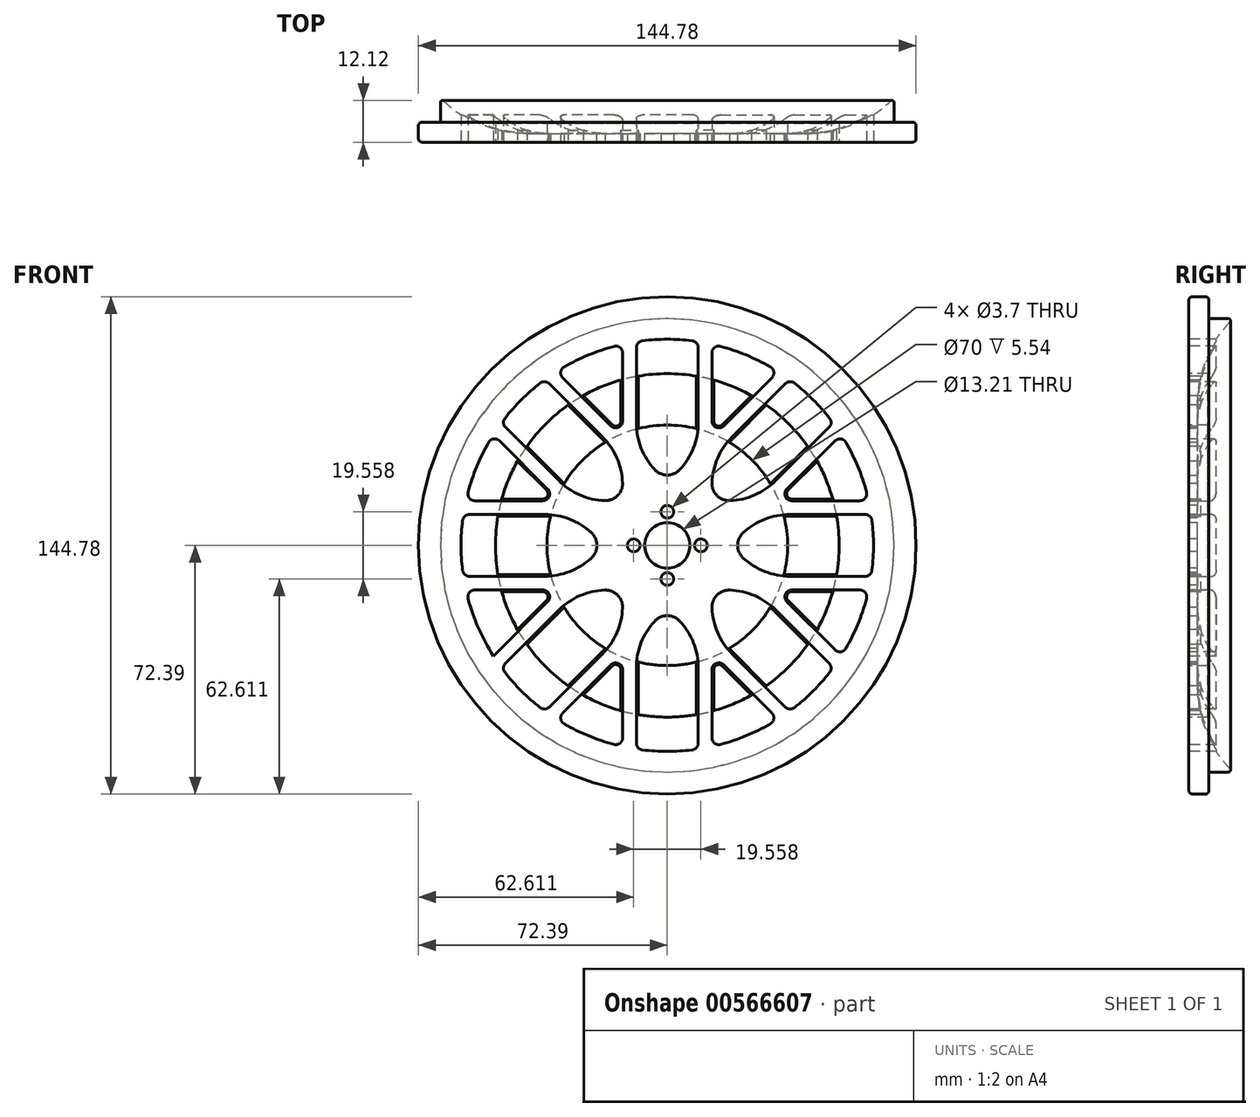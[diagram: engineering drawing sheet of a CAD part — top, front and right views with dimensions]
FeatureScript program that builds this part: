
annotation { "Feature Type Name" : "Feature", "Feature Type Description" : "" }
export const myFeature = defineFeature(function(context is Context, id is Id, definition is map)
    precondition{}
    {
        {
            var Q0;
            Q0=qCreatedBy(makeId("Right.planeOp"),FACE);
            var sketch = newSketch(context, id + "F0", { "sketchPlane" : qUnion([Q0])});
            skLineSegment(sketch, "E0", {"start": v(0, 6.6) * mm, "end": v(2.54, 6.6) * mm});
            skLineSegment(sketch, "E1", {"start": v(2.54, 6.6) * mm, "end": v(2.54, 42) * mm});
            skLineSegment(sketch, "E2", {"start": v(0, 6.6) * mm, "end": v(0, 66) * mm});
            skLineSegment(sketch, "E3", {"start": v(0, 66) * mm, "end": v(13, 66) * mm});
            skArc(sketch, "E4", {"start": v(2.54, 42) * mm, "mid": v(5.27, 55.1) * mm, "end": v(13, 66) * mm});
            skLineSegment(sketch, "E5", {"start": v(0, 0) * mm, "end": v(13, 0) * mm, "construction": true});
            skSolve(sketch);
        }
        {
            var Q0;
            Q0=makeQuery(id+"F0.imprint","IMPRINT",FACE,{"disambiguationData":[TD([[makeQuery(id+"F0.imprint","IMPRINT",EDGE,{"derivedFrom":sQuery(id+"F0.wireOp",EDGE,"E0")}),1.0]])]});
            var Q1;
            Q1=sQuery(id+"F0.wireOp",EDGE,"E5");
            revolve(context, id + "F1", {"entities" : qUnion([Q0]), "axis" : qUnion([Q1]), "revolveType" : RevolveType.FULL});
        }
        {
            var Q0;
            Q0=qCreatedBy(makeId("Front.planeOp"),FACE);
            var sketch = newSketch(context, id + "F2", { "sketchPlane" : qUnion([Q0])});
            skCircle(sketch, "E6", {"center": v(0, 0) * mm, "radius": 9.78 * mm, "construction": true});
            skPoint(sketch, "E7", {"position": v(0, 9.78) * mm});
            skPoint(sketch, "E8", {"position": v(0, -9.78) * mm});
            skPoint(sketch, "E9", {"position": v(9.78, 0) * mm});
            skPoint(sketch, "E10", {"position": v(-9.78, 0) * mm});
            skSolve(sketch);
        }
        {
            var Q0;
            Q0=sQuery(id+"F2.wireOp",VERTEX,"E7");
            var Q1;
            Q1=sQuery(id+"F2.wireOp",VERTEX,"E9");
            var Q2;
            Q2=sQuery(id+"F2.wireOp",VERTEX,"E8");
            var Q3;
            Q3=sQuery(id+"F2.wireOp",VERTEX,"E10");
            var Q4;
            Q4=makeQuery(id+"F1.opRevolve","SWEPT_BODY",BODY,{"disambiguationData":[OSD([sQuery(id+"F0.wireOp",EDGE,"E0"),sQuery(id+"F0.wireOp",EDGE,"E1"),sQuery(id+"F0.wireOp",EDGE,"E2"),sQuery(id+"F0.wireOp",EDGE,"E3"),sQuery(id+"F0.wireOp",EDGE,"E4")])]});
            hole(context, id + "F3", {"style" : HoleStyle.SIMPLE, "holeDiameter" : 3.7 * mm, "endStyle" : HoleEndStyle.THROUGH, "locations" : qUnion([Q0, Q1, Q2, Q3]), "scope" : qUnion([Q4])});
        }
        {
            var Q0;
            Q0=makeQuery(id+"F1.opRevolve","SWEPT_FACE",FACE,{"disambiguationData":[OSD([sQuery(id+"F0.wireOp",EDGE,"E2")])]});
            var sketch = newSketch(context, id + "F4", { "sketchPlane" : qUnion([Q0])});
            skArc(sketch, "E11", {"start": v(-35.58, 48.31) * mm, "mid": v(-42.43, 42.43) * mm, "end": v(-48.31, 35.58) * mm});
            skLineSegment(sketch, "E12", {"start": v(-58.57, 13) * mm, "end": v(-31.38, 13) * mm});
            skLineSegment(sketch, "E13", {"start": v(-58.57, -13) * mm, "end": v(-31.38, -13) * mm});
            skLineSegment(sketch, "E14", {"start": v(-13, 58.57) * mm, "end": v(-13, 31.38) * mm});
            skLineSegment(sketch, "E15", {"start": v(13, -58.57) * mm, "end": v(13, -31.38) * mm});
            skLineSegment(sketch, "E16", {"start": v(-50.61, 32.23) * mm, "end": v(-31.38, 13) * mm});
            skLineSegment(sketch, "E17", {"start": v(-32.23, 50.61) * mm, "end": v(-13, 31.38) * mm});
            skLineSegment(sketch, "E18", {"start": v(-50.61, -32.23) * mm, "end": v(-31.38, -13) * mm});
            skLineSegment(sketch, "E19", {"start": v(-32.23, -50.61) * mm, "end": v(-13, -31.38) * mm});
            skLineSegment(sketch, "E20.trimOffspring", {"start": v(0, 18.38) * mm, "end": v(9, 27.38) * mm});
            skLineSegment(sketch, "E21.trimOffspring", {"start": v(13, 13) * mm, "end": v(25.73, 13) * mm});
            skLineSegment(sketch, "E22.trimOffspring", {"start": v(18.38, 0) * mm, "end": v(27.38, -9) * mm});
            skLineSegment(sketch, "E23.trimOffspring", {"start": v(13, 13) * mm, "end": v(13, 25.73) * mm});
            skLineSegment(sketch, "E24.trimOffspring", {"start": v(18.38, 0) * mm, "end": v(27.38, 9) * mm});
            skLineSegment(sketch, "E25.trimOffspring", {"start": v(13, -13) * mm, "end": v(25.73, -13) * mm});
            skLineSegment(sketch, "E26.trimOffspring", {"start": v(0, -18.38) * mm, "end": v(9, -27.38) * mm});
            skLineSegment(sketch, "E27.trimOffspring", {"start": v(-13, -13) * mm, "end": v(-13, -25.73) * mm});
            skLineSegment(sketch, "E28.0", {"start": v(-35.58, 48.31) * mm, "end": v(-13, 25.73) * mm});
            skCircle(sketch, "E29.0", {"center": v(0, 0) * mm, "radius": 71 * mm});
            skLineSegment(sketch, "E30.0", {"start": v(-48.31, 35.58) * mm, "end": v(-25.73, 13) * mm});
            skLineSegment(sketch, "E31.0", {"start": v(-9, 59.32) * mm, "end": v(-9, 27.38) * mm});
            skLineSegment(sketch, "E32.0", {"start": v(9, 27.38) * mm, "end": v(9, 59.32) * mm});
            skLineSegment(sketch, "E33.0", {"start": v(13, 25.73) * mm, "end": v(35.58, 48.31) * mm});
            skLineSegment(sketch, "E34.0", {"start": v(25.73, 13) * mm, "end": v(48.31, 35.58) * mm});
            skLineSegment(sketch, "E35.0", {"start": v(27.38, 9) * mm, "end": v(59.32, 9) * mm});
            skLineSegment(sketch, "E36.0", {"start": v(27.38, -9) * mm, "end": v(59.32, -9) * mm});
            skLineSegment(sketch, "E37.0", {"start": v(25.73, -13) * mm, "end": v(48.31, -35.58) * mm});
            skLineSegment(sketch, "E38.0", {"start": v(13, -25.73) * mm, "end": v(35.58, -48.31) * mm});
            skLineSegment(sketch, "E39.0", {"start": v(9, -59.32) * mm, "end": v(9, -27.38) * mm});
            skLineSegment(sketch, "E40.0", {"start": v(-9, -27.38) * mm, "end": v(-9, -59.32) * mm});
            skLineSegment(sketch, "E41.0", {"start": v(-35.58, -48.31) * mm, "end": v(-13, -25.73) * mm});
            skLineSegment(sketch, "E42.0", {"start": v(-48.31, -35.58) * mm, "end": v(-25.73, -13) * mm});
            skLineSegment(sketch, "E43.0", {"start": v(-59.32, -9) * mm, "end": v(-27.38, -9) * mm});
            skLineSegment(sketch, "E44.0", {"start": v(-59.32, 9) * mm, "end": v(-27.38, 9) * mm});
            skLineSegment(sketch, "E45.trimOffspring", {"start": v(-25.73, 13) * mm, "end": v(-13, 13) * mm});
            skLineSegment(sketch, "E46.trimOffspring", {"start": v(-27.38, 9) * mm, "end": v(-18.38, 0) * mm});
            skLineSegment(sketch, "E47.trimOffspring", {"start": v(-27.38, -9) * mm, "end": v(-18.38, 0) * mm});
            skLineSegment(sketch, "E48.trimOffspring", {"start": v(-25.73, -13) * mm, "end": v(-13, -13) * mm});
            skLineSegment(sketch, "E49.trimOffspring", {"start": v(-9, -27.38) * mm, "end": v(0, -18.38) * mm});
            skLineSegment(sketch, "E50.trimOffspring", {"start": v(-13, -31.38) * mm, "end": v(-13, -58.57) * mm});
            skLineSegment(sketch, "E51.trimOffspring", {"start": v(13, -31.38) * mm, "end": v(32.23, -50.61) * mm});
            skLineSegment(sketch, "E52.trimOffspring", {"start": v(13, -25.73) * mm, "end": v(13, -13) * mm});
            skLineSegment(sketch, "E53.trimOffspring", {"start": v(31.38, -13) * mm, "end": v(50.61, -32.23) * mm});
            skLineSegment(sketch, "E54.trimOffspring", {"start": v(31.38, -13) * mm, "end": v(58.57, -13) * mm});
            skLineSegment(sketch, "E55.trimOffspring", {"start": v(31.38, 13) * mm, "end": v(50.61, 32.23) * mm});
            skLineSegment(sketch, "E56.trimOffspring", {"start": v(31.38, 13) * mm, "end": v(58.57, 13) * mm});
            skLineSegment(sketch, "E57.trimOffspring", {"start": v(13, 31.38) * mm, "end": v(13, 58.57) * mm});
            skLineSegment(sketch, "E58.trimOffspring", {"start": v(13, 31.38) * mm, "end": v(32.23, 50.61) * mm});
            skLineSegment(sketch, "E59.trimOffspring", {"start": v(-9, 27.38) * mm, "end": v(0, 18.38) * mm});
            skLineSegment(sketch, "E60.trimOffspring", {"start": v(-13, 25.73) * mm, "end": v(-13, 13) * mm});
            skArc(sketch, "E61.trimOffspring", {"start": v(-50.61, 32.23) * mm, "mid": v(-55.43, 22.96) * mm, "end": v(-58.57, 13) * mm});
            skArc(sketch, "E62.trimOffspring", {"start": v(-13, 58.57) * mm, "mid": v(-22.96, 55.43) * mm, "end": v(-32.23, 50.61) * mm});
            skArc(sketch, "E63.trimOffspring", {"start": v(9, 59.32) * mm, "mid": v(0, 60) * mm, "end": v(-9, 59.32) * mm});
            skArc(sketch, "E64.trimOffspring", {"start": v(32.23, 50.61) * mm, "mid": v(22.96, 55.43) * mm, "end": v(13, 58.57) * mm});
            skArc(sketch, "E65.trimOffspring", {"start": v(48.31, 35.58) * mm, "mid": v(42.43, 42.43) * mm, "end": v(35.58, 48.31) * mm});
            skArc(sketch, "E66.trimOffspring", {"start": v(58.57, 13) * mm, "mid": v(55.43, 22.96) * mm, "end": v(50.61, 32.23) * mm});
            skArc(sketch, "E67.trimOffspring", {"start": v(59.32, -9) * mm, "mid": v(60, 0) * mm, "end": v(59.32, 9) * mm});
            skArc(sketch, "E68.trimOffspring", {"start": v(50.61, -32.23) * mm, "mid": v(55.43, -22.96) * mm, "end": v(58.57, -13) * mm});
            skArc(sketch, "E69.trimOffspring", {"start": v(35.58, -48.31) * mm, "mid": v(42.43, -42.43) * mm, "end": v(48.31, -35.58) * mm});
            skArc(sketch, "E70.trimOffspring", {"start": v(13, -58.57) * mm, "mid": v(22.96, -55.43) * mm, "end": v(32.23, -50.61) * mm});
            skArc(sketch, "E71.trimOffspring", {"start": v(-9, -59.32) * mm, "mid": v(0, -60) * mm, "end": v(9, -59.32) * mm});
            skArc(sketch, "E72.trimOffspring", {"start": v(-32.23, -50.61) * mm, "mid": v(-22.96, -55.43) * mm, "end": v(-13, -58.57) * mm});
            skArc(sketch, "E73.trimOffspring", {"start": v(-48.31, -35.58) * mm, "mid": v(-42.43, -42.43) * mm, "end": v(-35.58, -48.31) * mm});
            skArc(sketch, "E74.trimOffspring", {"start": v(-58.57, -13) * mm, "mid": v(-55.43, -22.96) * mm, "end": v(-50.61, -32.23) * mm});
            skArc(sketch, "E75.trimOffspring", {"start": v(-59.32, 9) * mm, "mid": v(-60, 0) * mm, "end": v(-59.32, -9) * mm});
            skSolve(sketch);
        }
        {
            var Q0;
            Q0=makeQuery(id+"F4.imprint","IMPRINT",FACE,{"disambiguationData":[TD([[makeQuery(id+"F4.imprint","IMPRINT",EDGE,{"derivedFrom":sQuery(id+"F4.wireOp",EDGE,"E29.0")}),1.0]])]});
            var Q1;
            Q1=makeQuery(id+"F4.imprint","IMPRINT",FACE,{"disambiguationData":[TD([[makeQuery(id+"F4.imprint","IMPRINT",EDGE,{"derivedFrom":makeQuery(id+"F1.opRevolve","SWEPT_EDGE",EDGE,{"disambiguationData":[OSD([sQuery(id+"F0.wireOp",EDGE,"E0"),sQuery(id+"F0.wireOp",EDGE,"E2")])]})}),1.0]])]});
            var Q2;
            Q2=makeQuery(id+"F4.imprint","IMPRINT",FACE,{"disambiguationData":[TD([[makeQuery(id+"F4.imprint","IMPRINT",EDGE,{"derivedFrom":makeQuery(id+"F3.hole-0.boolean.opBoolean","COPY",EDGE,{"derivedFrom":makeQuery(id+"F3.hole-0.opRevolve","SWEPT_EDGE",EDGE,{"disambiguationData":[OSD([sQuery(id+"F3.hole-0.sketch.wireOp",EDGE,"core_line_2"),sQuery(id+"F3.hole-0.sketch.wireOp",EDGE,"core_line_3")])]})})}),1.0]])]});
            var Q3;
            Q3=makeQuery(id+"F4.imprint","IMPRINT",FACE,{"disambiguationData":[TD([[makeQuery(id+"F4.imprint","IMPRINT",EDGE,{"derivedFrom":makeQuery(id+"F3.hole-1.boolean.opBoolean","COPY",EDGE,{"derivedFrom":makeQuery(id+"F3.hole-1.opRevolve","SWEPT_EDGE",EDGE,{"disambiguationData":[OSD([sQuery(id+"F3.hole-1.sketch.wireOp",EDGE,"core_line_2"),sQuery(id+"F3.hole-1.sketch.wireOp",EDGE,"core_line_3")])]})})}),1.0]])]});
            var Q4;
            Q4=makeQuery(id+"F4.imprint","IMPRINT",FACE,{"disambiguationData":[TD([[makeQuery(id+"F4.imprint","IMPRINT",EDGE,{"derivedFrom":makeQuery(id+"F3.hole-2.boolean.opBoolean","COPY",EDGE,{"derivedFrom":makeQuery(id+"F3.hole-2.opRevolve","SWEPT_EDGE",EDGE,{"disambiguationData":[OSD([sQuery(id+"F3.hole-2.sketch.wireOp",EDGE,"core_line_2"),sQuery(id+"F3.hole-2.sketch.wireOp",EDGE,"core_line_3")])]})})}),1.0]])]});
            var Q5;
            Q5=makeQuery(id+"F4.imprint","IMPRINT",FACE,{"disambiguationData":[TD([[makeQuery(id+"F4.imprint","IMPRINT",EDGE,{"derivedFrom":makeQuery(id+"F3.hole-3.boolean.opBoolean","COPY",EDGE,{"derivedFrom":makeQuery(id+"F3.hole-3.opRevolve","SWEPT_EDGE",EDGE,{"disambiguationData":[OSD([sQuery(id+"F3.hole-3.sketch.wireOp",EDGE,"core_line_2"),sQuery(id+"F3.hole-3.sketch.wireOp",EDGE,"core_line_3")])]})})}),1.0]])]});
            var Q6;
            Q6=makeQuery(id+"F4.imprint","IMPRINT",FACE,{"disambiguationData":[TD([[makeQuery(id+"F4.imprint","IMPRINT",EDGE,{"derivedFrom":sQuery(id+"F4.wireOp",EDGE,"E11")}),1.0]])]});
            var Q7;
            Q7=makeQuery(id+"F4.imprint","IMPRINT",FACE,{"disambiguationData":[TD([[makeQuery(id+"F4.imprint","IMPRINT",EDGE,{"derivedFrom":sQuery(id+"F4.wireOp",EDGE,"E12")}),1.0]])]});
            var Q8;
            Q8=makeQuery(id+"F4.imprint","IMPRINT",FACE,{"disambiguationData":[TD([[makeQuery(id+"F4.imprint","IMPRINT",EDGE,{"derivedFrom":sQuery(id+"F4.wireOp",EDGE,"E43.0")}),1.0]])]});
            var Q9;
            Q9=makeQuery(id+"F4.imprint","IMPRINT",FACE,{"disambiguationData":[TD([[makeQuery(id+"F4.imprint","IMPRINT",EDGE,{"derivedFrom":sQuery(id+"F4.wireOp",EDGE,"E13")}),-1.0]])]});
            var Q10;
            Q10=makeQuery(id+"F4.imprint","IMPRINT",FACE,{"disambiguationData":[TD([[makeQuery(id+"F4.imprint","IMPRINT",EDGE,{"derivedFrom":sQuery(id+"F4.wireOp",EDGE,"E27.trimOffspring")}),-1.0]])]});
            var Q11;
            Q11=makeQuery(id+"F4.imprint","IMPRINT",FACE,{"disambiguationData":[TD([[makeQuery(id+"F4.imprint","IMPRINT",EDGE,{"derivedFrom":sQuery(id+"F4.wireOp",EDGE,"E26.trimOffspring")}),-1.0]])]});
            var Q12;
            Q12=makeQuery(id+"F4.imprint","IMPRINT",FACE,{"disambiguationData":[TD([[makeQuery(id+"F4.imprint","IMPRINT",EDGE,{"derivedFrom":sQuery(id+"F4.wireOp",EDGE,"E15")}),-1.0]])]});
            var Q13;
            Q13=makeQuery(id+"F4.imprint","IMPRINT",FACE,{"disambiguationData":[TD([[makeQuery(id+"F4.imprint","IMPRINT",EDGE,{"derivedFrom":sQuery(id+"F4.wireOp",EDGE,"E25.trimOffspring")}),-1.0]])]});
            var Q14;
            Q14=makeQuery(id+"F4.imprint","IMPRINT",FACE,{"disambiguationData":[TD([[makeQuery(id+"F4.imprint","IMPRINT",EDGE,{"derivedFrom":sQuery(id+"F4.wireOp",EDGE,"E53.trimOffspring")}),1.0]])]});
            var Q15;
            Q15=makeQuery(id+"F4.imprint","IMPRINT",FACE,{"disambiguationData":[TD([[makeQuery(id+"F4.imprint","IMPRINT",EDGE,{"derivedFrom":sQuery(id+"F4.wireOp",EDGE,"E22.trimOffspring")}),1.0]])]});
            var Q16;
            Q16=makeQuery(id+"F4.imprint","IMPRINT",FACE,{"disambiguationData":[TD([[makeQuery(id+"F4.imprint","IMPRINT",EDGE,{"derivedFrom":sQuery(id+"F4.wireOp",EDGE,"E55.trimOffspring")}),-1.0]])]});
            var Q17;
            Q17=makeQuery(id+"F4.imprint","IMPRINT",FACE,{"disambiguationData":[TD([[makeQuery(id+"F4.imprint","IMPRINT",EDGE,{"derivedFrom":sQuery(id+"F4.wireOp",EDGE,"E21.trimOffspring")}),1.0]])]});
            var Q18;
            Q18=makeQuery(id+"F4.imprint","IMPRINT",FACE,{"disambiguationData":[TD([[makeQuery(id+"F4.imprint","IMPRINT",EDGE,{"derivedFrom":sQuery(id+"F4.wireOp",EDGE,"E57.trimOffspring")}),-1.0]])]});
            var Q19;
            Q19=makeQuery(id+"F4.imprint","IMPRINT",FACE,{"disambiguationData":[TD([[makeQuery(id+"F4.imprint","IMPRINT",EDGE,{"derivedFrom":sQuery(id+"F4.wireOp",EDGE,"E20.trimOffspring")}),1.0]])]});
            var Q20;
            Q20=makeQuery(id+"F4.imprint","IMPRINT",FACE,{"disambiguationData":[TD([[makeQuery(id+"F4.imprint","IMPRINT",EDGE,{"derivedFrom":sQuery(id+"F4.wireOp",EDGE,"E14")}),-1.0]])]});
            var Q21;
            Q21=makeQuery(id+"F4.imprint","IMPRINT",FACE,{"disambiguationData":[TD([[makeQuery(id+"F4.imprint","IMPRINT",EDGE,{"derivedFrom":sQuery(id+"F4.wireOp",EDGE,"E19")}),-1.0]])]});
            extrude(context, id + "F5", {"entities" : qUnion([Q0, Q1, Q2, Q3, Q4, Q5, Q6, Q7, Q8, Q9, Q10, Q11, Q12, Q13, Q14, Q15, Q16, Q17, Q18, Q19, Q20, Q21]), "operationType" : NewBodyOperationType.REMOVE, "endBound" : BoundingType.THROUGH_ALL, "oppositeDirection" : true, "depth" : 25 * mm});
        }
        {
            var Q0;
            Q0=makeQuery(id+"F5.boolean.opBoolean","COPY",EDGE,{"derivedFrom":makeQuery(id+"F5.opExtrude","SWEPT_EDGE",EDGE,{"disambiguationData":[OSD([sQuery(id+"F4.wireOp",EDGE,"E31.0"),sQuery(id+"F4.wireOp",EDGE,"E59.trimOffspring")])]})});
            var Q1;
            Q1=makeQuery(id+"F5.boolean.opBoolean","COPY",EDGE,{"derivedFrom":makeQuery(id+"F5.opExtrude","SWEPT_EDGE",EDGE,{"disambiguationData":[OSD([sQuery(id+"F4.wireOp",EDGE,"E20.trimOffspring"),sQuery(id+"F4.wireOp",EDGE,"E32.0")])]})});
            var Q2;
            Q2=makeQuery(id+"F5.boolean.opBoolean","COPY",EDGE,{"derivedFrom":makeQuery(id+"F5.opExtrude","SWEPT_EDGE",EDGE,{"disambiguationData":[OSD([sQuery(id+"F4.wireOp",EDGE,"E23.trimOffspring"),sQuery(id+"F4.wireOp",EDGE,"E33.0")])]})});
            var Q3;
            Q3=makeQuery(id+"F5.boolean.opBoolean","COPY",EDGE,{"derivedFrom":makeQuery(id+"F5.opExtrude","SWEPT_EDGE",EDGE,{"disambiguationData":[OSD([sQuery(id+"F4.wireOp",EDGE,"E21.trimOffspring"),sQuery(id+"F4.wireOp",EDGE,"E34.0")])]})});
            var Q4;
            Q4=makeQuery(id+"F5.boolean.opBoolean","COPY",EDGE,{"derivedFrom":makeQuery(id+"F5.opExtrude","SWEPT_EDGE",EDGE,{"disambiguationData":[OSD([sQuery(id+"F4.wireOp",EDGE,"E24.trimOffspring"),sQuery(id+"F4.wireOp",EDGE,"E35.0")])]})});
            var Q5;
            Q5=makeQuery(id+"F5.boolean.opBoolean","COPY",EDGE,{"derivedFrom":makeQuery(id+"F5.opExtrude","SWEPT_EDGE",EDGE,{"disambiguationData":[OSD([sQuery(id+"F4.wireOp",EDGE,"E22.trimOffspring"),sQuery(id+"F4.wireOp",EDGE,"E36.0")])]})});
            var Q6;
            Q6=makeQuery(id+"F5.boolean.opBoolean","COPY",EDGE,{"derivedFrom":makeQuery(id+"F5.opExtrude","SWEPT_EDGE",EDGE,{"disambiguationData":[OSD([sQuery(id+"F4.wireOp",EDGE,"E25.trimOffspring"),sQuery(id+"F4.wireOp",EDGE,"E37.0")])]})});
            var Q7;
            Q7=makeQuery(id+"F5.boolean.opBoolean","COPY",EDGE,{"derivedFrom":makeQuery(id+"F5.opExtrude","SWEPT_EDGE",EDGE,{"disambiguationData":[OSD([sQuery(id+"F4.wireOp",EDGE,"E26.trimOffspring"),sQuery(id+"F4.wireOp",EDGE,"E39.0")])]})});
            var Q8;
            Q8=makeQuery(id+"F5.boolean.opBoolean","COPY",EDGE,{"derivedFrom":makeQuery(id+"F5.opExtrude","SWEPT_EDGE",EDGE,{"disambiguationData":[OSD([sQuery(id+"F4.wireOp",EDGE,"E38.0"),sQuery(id+"F4.wireOp",EDGE,"E52.trimOffspring")])]})});
            var Q9;
            Q9=makeQuery(id+"F5.boolean.opBoolean","COPY",EDGE,{"derivedFrom":makeQuery(id+"F5.opExtrude","SWEPT_EDGE",EDGE,{"disambiguationData":[OSD([sQuery(id+"F4.wireOp",EDGE,"E40.0"),sQuery(id+"F4.wireOp",EDGE,"E49.trimOffspring")])]})});
            var Q10;
            Q10=makeQuery(id+"F5.boolean.opBoolean","COPY",EDGE,{"derivedFrom":makeQuery(id+"F5.opExtrude","SWEPT_EDGE",EDGE,{"disambiguationData":[OSD([sQuery(id+"F4.wireOp",EDGE,"E27.trimOffspring"),sQuery(id+"F4.wireOp",EDGE,"E41.0")])]})});
            var Q11;
            Q11=makeQuery(id+"F5.boolean.opBoolean","COPY",EDGE,{"derivedFrom":makeQuery(id+"F5.opExtrude","SWEPT_EDGE",EDGE,{"disambiguationData":[OSD([sQuery(id+"F4.wireOp",EDGE,"E43.0"),sQuery(id+"F4.wireOp",EDGE,"E47.trimOffspring")])]})});
            var Q12;
            Q12=makeQuery(id+"F5.boolean.opBoolean","COPY",EDGE,{"derivedFrom":makeQuery(id+"F5.opExtrude","SWEPT_EDGE",EDGE,{"disambiguationData":[OSD([sQuery(id+"F4.wireOp",EDGE,"E42.0"),sQuery(id+"F4.wireOp",EDGE,"E48.trimOffspring")])]})});
            var Q13;
            Q13=makeQuery(id+"F5.boolean.opBoolean","COPY",EDGE,{"derivedFrom":makeQuery(id+"F5.opExtrude","SWEPT_EDGE",EDGE,{"disambiguationData":[OSD([sQuery(id+"F4.wireOp",EDGE,"E44.0"),sQuery(id+"F4.wireOp",EDGE,"E46.trimOffspring")])]})});
            var Q14;
            Q14=makeQuery(id+"F5.boolean.opBoolean","COPY",EDGE,{"derivedFrom":makeQuery(id+"F5.opExtrude","SWEPT_EDGE",EDGE,{"disambiguationData":[OSD([sQuery(id+"F4.wireOp",EDGE,"E28.0"),sQuery(id+"F4.wireOp",EDGE,"E60.trimOffspring")])]})});
            var Q15;
            Q15=makeQuery(id+"F5.boolean.opBoolean","COPY",EDGE,{"derivedFrom":makeQuery(id+"F5.opExtrude","SWEPT_EDGE",EDGE,{"disambiguationData":[OSD([sQuery(id+"F4.wireOp",EDGE,"E30.0"),sQuery(id+"F4.wireOp",EDGE,"E45.trimOffspring")])]})});
            fillet(context, id + "F6", {"entities" : qUnion([Q0, Q1, Q2, Q3, Q4, Q5, Q6, Q7, Q8, Q9, Q10, Q11, Q12, Q13, Q14, Q15]), "radius" : 20 * mm, "tangentPropagation" : true, "allowEdgeOverflow" : false});
        }
        {
            var Q0;
            Q0=makeQuery(id+"F5.boolean.opBoolean","COPY",EDGE,{"derivedFrom":makeQuery(id+"F5.opExtrude","SWEPT_EDGE",EDGE,{"disambiguationData":[OSD([sQuery(id+"F4.wireOp",EDGE,"E22.trimOffspring"),sQuery(id+"F4.wireOp",EDGE,"E24.trimOffspring")])]})});
            var Q1;
            Q1=makeQuery(id+"F5.boolean.opBoolean","COPY",EDGE,{"derivedFrom":makeQuery(id+"F5.opExtrude","SWEPT_EDGE",EDGE,{"disambiguationData":[OSD([sQuery(id+"F4.wireOp",EDGE,"E21.trimOffspring"),sQuery(id+"F4.wireOp",EDGE,"E23.trimOffspring")])]})});
            var Q2;
            Q2=makeQuery(id+"F5.boolean.opBoolean","COPY",EDGE,{"derivedFrom":makeQuery(id+"F5.opExtrude","SWEPT_EDGE",EDGE,{"disambiguationData":[OSD([sQuery(id+"F4.wireOp",EDGE,"E20.trimOffspring"),sQuery(id+"F4.wireOp",EDGE,"E59.trimOffspring")])]})});
            var Q3;
            Q3=makeQuery(id+"F5.boolean.opBoolean","COPY",EDGE,{"derivedFrom":makeQuery(id+"F5.opExtrude","SWEPT_EDGE",EDGE,{"disambiguationData":[OSD([sQuery(id+"F4.wireOp",EDGE,"E45.trimOffspring"),sQuery(id+"F4.wireOp",EDGE,"E60.trimOffspring")])]})});
            var Q4;
            Q4=makeQuery(id+"F5.boolean.opBoolean","COPY",EDGE,{"derivedFrom":makeQuery(id+"F5.opExtrude","SWEPT_EDGE",EDGE,{"disambiguationData":[OSD([sQuery(id+"F4.wireOp",EDGE,"E46.trimOffspring"),sQuery(id+"F4.wireOp",EDGE,"E47.trimOffspring")])]})});
            var Q5;
            Q5=makeQuery(id+"F5.boolean.opBoolean","COPY",EDGE,{"derivedFrom":makeQuery(id+"F5.opExtrude","SWEPT_EDGE",EDGE,{"disambiguationData":[OSD([sQuery(id+"F4.wireOp",EDGE,"E27.trimOffspring"),sQuery(id+"F4.wireOp",EDGE,"E48.trimOffspring")])]})});
            var Q6;
            Q6=makeQuery(id+"F5.boolean.opBoolean","COPY",EDGE,{"derivedFrom":makeQuery(id+"F5.opExtrude","SWEPT_EDGE",EDGE,{"disambiguationData":[OSD([sQuery(id+"F4.wireOp",EDGE,"E26.trimOffspring"),sQuery(id+"F4.wireOp",EDGE,"E49.trimOffspring")])]})});
            var Q7;
            Q7=makeQuery(id+"F5.boolean.opBoolean","COPY",EDGE,{"derivedFrom":makeQuery(id+"F5.opExtrude","SWEPT_EDGE",EDGE,{"disambiguationData":[OSD([sQuery(id+"F4.wireOp",EDGE,"E25.trimOffspring"),sQuery(id+"F4.wireOp",EDGE,"E52.trimOffspring")])]})});
            fillet(context, id + "F7", {"entities" : qUnion([Q0, Q1, Q2, Q3, Q4, Q5, Q6, Q7]), "radius" : 5 * mm, "tangentPropagation" : true, "allowEdgeOverflow" : false});
        }
        {
            var Q0;
            Q0=makeQuery(id+"F5.boolean.opBoolean","COPY",EDGE,{"derivedFrom":makeQuery(id+"F5.opExtrude","SWEPT_EDGE",EDGE,{"disambiguationData":[OSD([sQuery(id+"F4.wireOp",EDGE,"E12"),sQuery(id+"F4.wireOp",EDGE,"E16")])]})});
            var Q1;
            Q1=makeQuery(id+"F5.boolean.opBoolean","COPY",EDGE,{"derivedFrom":makeQuery(id+"F5.opExtrude","SWEPT_EDGE",EDGE,{"disambiguationData":[OSD([sQuery(id+"F4.wireOp",EDGE,"E14"),sQuery(id+"F4.wireOp",EDGE,"E17")])]})});
            var Q2;
            Q2=makeQuery(id+"F5.boolean.opBoolean","COPY",EDGE,{"derivedFrom":makeQuery(id+"F5.opExtrude","SWEPT_EDGE",EDGE,{"disambiguationData":[OSD([sQuery(id+"F4.wireOp",EDGE,"E57.trimOffspring"),sQuery(id+"F4.wireOp",EDGE,"E58.trimOffspring")])]})});
            var Q3;
            Q3=makeQuery(id+"F5.boolean.opBoolean","COPY",EDGE,{"derivedFrom":makeQuery(id+"F5.opExtrude","SWEPT_EDGE",EDGE,{"disambiguationData":[OSD([sQuery(id+"F4.wireOp",EDGE,"E55.trimOffspring"),sQuery(id+"F4.wireOp",EDGE,"E56.trimOffspring")])]})});
            var Q4;
            Q4=makeQuery(id+"F5.boolean.opBoolean","COPY",EDGE,{"derivedFrom":makeQuery(id+"F5.opExtrude","SWEPT_EDGE",EDGE,{"disambiguationData":[OSD([sQuery(id+"F4.wireOp",EDGE,"E53.trimOffspring"),sQuery(id+"F4.wireOp",EDGE,"E54.trimOffspring")])]})});
            var Q5;
            Q5=makeQuery(id+"F5.boolean.opBoolean","COPY",EDGE,{"derivedFrom":makeQuery(id+"F5.opExtrude","SWEPT_EDGE",EDGE,{"disambiguationData":[OSD([sQuery(id+"F4.wireOp",EDGE,"E15"),sQuery(id+"F4.wireOp",EDGE,"E51.trimOffspring")])]})});
            var Q6;
            Q6=makeQuery(id+"F5.boolean.opBoolean","COPY",EDGE,{"derivedFrom":makeQuery(id+"F5.opExtrude","SWEPT_EDGE",EDGE,{"disambiguationData":[OSD([sQuery(id+"F4.wireOp",EDGE,"E19"),sQuery(id+"F4.wireOp",EDGE,"E50.trimOffspring")])]})});
            var Q7;
            Q7=makeQuery(id+"F5.boolean.opBoolean","COPY",EDGE,{"derivedFrom":makeQuery(id+"F5.opExtrude","SWEPT_EDGE",EDGE,{"disambiguationData":[OSD([sQuery(id+"F4.wireOp",EDGE,"E13"),sQuery(id+"F4.wireOp",EDGE,"E18")])]})});
            var Q8;
            Q8=makeQuery(id+"F5.boolean.opBoolean","COPY",EDGE,{"derivedFrom":makeQuery(id+"F5.opExtrude","SWEPT_EDGE",EDGE,{"disambiguationData":[OSD([sQuery(id+"F4.wireOp",EDGE,"E14"),sQuery(id+"F4.wireOp",EDGE,"E62.trimOffspring")])]})});
            var Q9;
            Q9=makeQuery(id+"F5.boolean.opBoolean","COPY",EDGE,{"derivedFrom":makeQuery(id+"F5.opExtrude","SWEPT_EDGE",EDGE,{"disambiguationData":[OSD([sQuery(id+"F4.wireOp",EDGE,"E31.0"),sQuery(id+"F4.wireOp",EDGE,"E63.trimOffspring")])]})});
            var Q10;
            Q10=makeQuery(id+"F5.boolean.opBoolean","COPY",EDGE,{"derivedFrom":makeQuery(id+"F5.opExtrude","SWEPT_EDGE",EDGE,{"disambiguationData":[OSD([sQuery(id+"F4.wireOp",EDGE,"E17"),sQuery(id+"F4.wireOp",EDGE,"E62.trimOffspring")])]})});
            var Q11;
            Q11=makeQuery(id+"F5.boolean.opBoolean","COPY",EDGE,{"derivedFrom":makeQuery(id+"F5.opExtrude","SWEPT_EDGE",EDGE,{"disambiguationData":[OSD([sQuery(id+"F4.wireOp",EDGE,"E11"),sQuery(id+"F4.wireOp",EDGE,"E28.0")])]})});
            var Q12;
            Q12=makeQuery(id+"F5.boolean.opBoolean","COPY",EDGE,{"derivedFrom":makeQuery(id+"F5.opExtrude","SWEPT_EDGE",EDGE,{"disambiguationData":[OSD([sQuery(id+"F4.wireOp",EDGE,"E11"),sQuery(id+"F4.wireOp",EDGE,"E30.0")])]})});
            var Q13;
            Q13=makeQuery(id+"F5.boolean.opBoolean","COPY",EDGE,{"derivedFrom":makeQuery(id+"F5.opExtrude","SWEPT_EDGE",EDGE,{"disambiguationData":[OSD([sQuery(id+"F4.wireOp",EDGE,"E16"),sQuery(id+"F4.wireOp",EDGE,"E61.trimOffspring")])]})});
            var Q14;
            Q14=makeQuery(id+"F5.boolean.opBoolean","COPY",EDGE,{"derivedFrom":makeQuery(id+"F5.opExtrude","SWEPT_EDGE",EDGE,{"disambiguationData":[OSD([sQuery(id+"F4.wireOp",EDGE,"E12"),sQuery(id+"F4.wireOp",EDGE,"E61.trimOffspring")])]})});
            var Q15;
            Q15=makeQuery(id+"F5.boolean.opBoolean","COPY",EDGE,{"derivedFrom":makeQuery(id+"F5.opExtrude","SWEPT_EDGE",EDGE,{"disambiguationData":[OSD([sQuery(id+"F4.wireOp",EDGE,"E43.0"),sQuery(id+"F4.wireOp",EDGE,"E75.trimOffspring")])]})});
            var Q16;
            Q16=makeQuery(id+"F5.boolean.opBoolean","COPY",EDGE,{"derivedFrom":makeQuery(id+"F5.opExtrude","SWEPT_EDGE",EDGE,{"disambiguationData":[OSD([sQuery(id+"F4.wireOp",EDGE,"E13"),sQuery(id+"F4.wireOp",EDGE,"E74.trimOffspring")])]})});
            var Q17;
            Q17=makeQuery(id+"F5.boolean.opBoolean","COPY",EDGE,{"derivedFrom":makeQuery(id+"F5.opExtrude","SWEPT_EDGE",EDGE,{"disambiguationData":[OSD([sQuery(id+"F4.wireOp",EDGE,"E42.0"),sQuery(id+"F4.wireOp",EDGE,"E73.trimOffspring")])]})});
            var Q18;
            Q18=makeQuery(id+"F5.boolean.opBoolean","COPY",EDGE,{"derivedFrom":makeQuery(id+"F5.opExtrude","SWEPT_EDGE",EDGE,{"disambiguationData":[OSD([sQuery(id+"F4.wireOp",EDGE,"E44.0"),sQuery(id+"F4.wireOp",EDGE,"E75.trimOffspring")])]})});
            var Q19;
            Q19=makeQuery(id+"F5.boolean.opBoolean","COPY",EDGE,{"derivedFrom":makeQuery(id+"F5.opExtrude","SWEPT_EDGE",EDGE,{"disambiguationData":[OSD([sQuery(id+"F4.wireOp",EDGE,"E41.0"),sQuery(id+"F4.wireOp",EDGE,"E73.trimOffspring")])]})});
            var Q20;
            Q20=makeQuery(id+"F5.boolean.opBoolean","COPY",EDGE,{"derivedFrom":makeQuery(id+"F5.opExtrude","SWEPT_EDGE",EDGE,{"disambiguationData":[OSD([sQuery(id+"F4.wireOp",EDGE,"E19"),sQuery(id+"F4.wireOp",EDGE,"E72.trimOffspring")])]})});
            var Q21;
            Q21=makeQuery(id+"F5.boolean.opBoolean","COPY",EDGE,{"derivedFrom":makeQuery(id+"F5.opExtrude","SWEPT_EDGE",EDGE,{"disambiguationData":[OSD([sQuery(id+"F4.wireOp",EDGE,"E40.0"),sQuery(id+"F4.wireOp",EDGE,"E71.trimOffspring")])]})});
            var Q22;
            Q22=makeQuery(id+"F5.boolean.opBoolean","COPY",EDGE,{"derivedFrom":makeQuery(id+"F5.opExtrude","SWEPT_EDGE",EDGE,{"disambiguationData":[OSD([sQuery(id+"F4.wireOp",EDGE,"E15"),sQuery(id+"F4.wireOp",EDGE,"E70.trimOffspring")])]})});
            var Q23;
            Q23=makeQuery(id+"F5.boolean.opBoolean","COPY",EDGE,{"derivedFrom":makeQuery(id+"F5.opExtrude","SWEPT_EDGE",EDGE,{"disambiguationData":[OSD([sQuery(id+"F4.wireOp",EDGE,"E50.trimOffspring"),sQuery(id+"F4.wireOp",EDGE,"E72.trimOffspring")])]})});
            var Q24;
            Q24=makeQuery(id+"F5.boolean.opBoolean","COPY",EDGE,{"derivedFrom":makeQuery(id+"F5.opExtrude","SWEPT_EDGE",EDGE,{"disambiguationData":[OSD([sQuery(id+"F4.wireOp",EDGE,"E39.0"),sQuery(id+"F4.wireOp",EDGE,"E71.trimOffspring")])]})});
            var Q25;
            Q25=makeQuery(id+"F5.boolean.opBoolean","COPY",EDGE,{"derivedFrom":makeQuery(id+"F5.opExtrude","SWEPT_EDGE",EDGE,{"disambiguationData":[OSD([sQuery(id+"F4.wireOp",EDGE,"E51.trimOffspring"),sQuery(id+"F4.wireOp",EDGE,"E70.trimOffspring")])]})});
            var Q26;
            Q26=makeQuery(id+"F5.boolean.opBoolean","COPY",EDGE,{"derivedFrom":makeQuery(id+"F5.opExtrude","SWEPT_EDGE",EDGE,{"disambiguationData":[OSD([sQuery(id+"F4.wireOp",EDGE,"E37.0"),sQuery(id+"F4.wireOp",EDGE,"E69.trimOffspring")])]})});
            var Q27;
            Q27=makeQuery(id+"F5.boolean.opBoolean","COPY",EDGE,{"derivedFrom":makeQuery(id+"F5.opExtrude","SWEPT_EDGE",EDGE,{"disambiguationData":[OSD([sQuery(id+"F4.wireOp",EDGE,"E36.0"),sQuery(id+"F4.wireOp",EDGE,"E67.trimOffspring")])]})});
            var Q28;
            Q28=makeQuery(id+"F5.boolean.opBoolean","COPY",EDGE,{"derivedFrom":makeQuery(id+"F5.opExtrude","SWEPT_EDGE",EDGE,{"disambiguationData":[OSD([sQuery(id+"F4.wireOp",EDGE,"E38.0"),sQuery(id+"F4.wireOp",EDGE,"E69.trimOffspring")])]})});
            var Q29;
            Q29=makeQuery(id+"F5.boolean.opBoolean","COPY",EDGE,{"derivedFrom":makeQuery(id+"F5.opExtrude","SWEPT_EDGE",EDGE,{"disambiguationData":[OSD([sQuery(id+"F4.wireOp",EDGE,"E53.trimOffspring"),sQuery(id+"F4.wireOp",EDGE,"E68.trimOffspring")])]})});
            var Q30;
            Q30=makeQuery(id+"F5.boolean.opBoolean","COPY",EDGE,{"derivedFrom":makeQuery(id+"F5.opExtrude","SWEPT_EDGE",EDGE,{"disambiguationData":[OSD([sQuery(id+"F4.wireOp",EDGE,"E54.trimOffspring"),sQuery(id+"F4.wireOp",EDGE,"E68.trimOffspring")])]})});
            var Q31;
            Q31=makeQuery(id+"F5.boolean.opBoolean","COPY",EDGE,{"derivedFrom":makeQuery(id+"F5.opExtrude","SWEPT_EDGE",EDGE,{"disambiguationData":[OSD([sQuery(id+"F4.wireOp",EDGE,"E35.0"),sQuery(id+"F4.wireOp",EDGE,"E67.trimOffspring")])]})});
            var Q32;
            Q32=makeQuery(id+"F5.boolean.opBoolean","COPY",EDGE,{"derivedFrom":makeQuery(id+"F5.opExtrude","SWEPT_EDGE",EDGE,{"disambiguationData":[OSD([sQuery(id+"F4.wireOp",EDGE,"E56.trimOffspring"),sQuery(id+"F4.wireOp",EDGE,"E66.trimOffspring")])]})});
            var Q33;
            Q33=makeQuery(id+"F5.boolean.opBoolean","COPY",EDGE,{"derivedFrom":makeQuery(id+"F5.opExtrude","SWEPT_EDGE",EDGE,{"disambiguationData":[OSD([sQuery(id+"F4.wireOp",EDGE,"E55.trimOffspring"),sQuery(id+"F4.wireOp",EDGE,"E66.trimOffspring")])]})});
            var Q34;
            Q34=makeQuery(id+"F5.boolean.opBoolean","COPY",EDGE,{"derivedFrom":makeQuery(id+"F5.opExtrude","SWEPT_EDGE",EDGE,{"disambiguationData":[OSD([sQuery(id+"F4.wireOp",EDGE,"E34.0"),sQuery(id+"F4.wireOp",EDGE,"E65.trimOffspring")])]})});
            var Q35;
            Q35=makeQuery(id+"F5.boolean.opBoolean","COPY",EDGE,{"derivedFrom":makeQuery(id+"F5.opExtrude","SWEPT_EDGE",EDGE,{"disambiguationData":[OSD([sQuery(id+"F4.wireOp",EDGE,"E33.0"),sQuery(id+"F4.wireOp",EDGE,"E65.trimOffspring")])]})});
            var Q36;
            Q36=makeQuery(id+"F5.boolean.opBoolean","COPY",EDGE,{"derivedFrom":makeQuery(id+"F5.opExtrude","SWEPT_EDGE",EDGE,{"disambiguationData":[OSD([sQuery(id+"F4.wireOp",EDGE,"E58.trimOffspring"),sQuery(id+"F4.wireOp",EDGE,"E64.trimOffspring")])]})});
            var Q37;
            Q37=makeQuery(id+"F5.boolean.opBoolean","COPY",EDGE,{"derivedFrom":makeQuery(id+"F5.opExtrude","SWEPT_EDGE",EDGE,{"disambiguationData":[OSD([sQuery(id+"F4.wireOp",EDGE,"E57.trimOffspring"),sQuery(id+"F4.wireOp",EDGE,"E64.trimOffspring")])]})});
            var Q38;
            Q38=makeQuery(id+"F5.boolean.opBoolean","COPY",EDGE,{"derivedFrom":makeQuery(id+"F5.opExtrude","SWEPT_EDGE",EDGE,{"disambiguationData":[OSD([sQuery(id+"F4.wireOp",EDGE,"E32.0"),sQuery(id+"F4.wireOp",EDGE,"E63.trimOffspring")])]})});
            fillet(context, id + "F8", {"entities" : qUnion([Q0, Q1, Q2, Q3, Q4, Q5, Q6, Q7, Q8, Q9, Q10, Q11, Q12, Q13, Q14, Q15, Q16, Q17, Q18, Q19, Q20, Q21, Q22, Q23, Q24, Q25, Q26, Q27, Q28, Q29, Q30, Q31, Q32, Q33, Q34, Q35, Q36, Q37, Q38]), "radius" : 2 * mm, "tangentPropagation" : true, "allowEdgeOverflow" : false});
        }
        {
            var Q0;
            Q0=makeQuery(id+"F1.opRevolve","SWEPT_EDGE",EDGE,{"disambiguationData":[OSD([sQuery(id+"F0.wireOp",EDGE,"E3"),sQuery(id+"F0.wireOp",EDGE,"E4")])]});
            fillet(context, id + "F9", {"entities" : qUnion([Q0]), "radius" : .6 * mm, "tangentPropagation" : true, "allowEdgeOverflow" : false});
        }
        {
            var Q0;
            Q0=qCreatedBy(makeId("Right.planeOp"),FACE);
            var sketch = newSketch(context, id + "F10", { "sketchPlane" : qUnion([Q0])});
            skArc(sketch, "E76", {"start": v(3.53, 50) * mm, "mid": v(2.79, 46.03) * mm, "end": v(2.54, 42) * mm});
            skLineSegment(sketch, "E77", {"start": v(2.54, 35) * mm, "end": v(2.54, 42) * mm});
            skLineSegment(sketch, "E78", {"start": v(2.54, 35) * mm, "end": v(5.54, 35) * mm});
            skLineSegment(sketch, "E79", {"start": v(5.54, 35) * mm, "end": v(5.54, 50) * mm});
            skLineSegment(sketch, "E80", {"start": v(5.54, 50) * mm, "end": v(3.53, 50) * mm});
            skLineSegment(sketch, "E81", {"start": v(0, 0) * mm, "end": v(5.54, 0) * mm, "construction": true});
            skSolve(sketch);
        }
        {
            var Q0;
            Q0=qSketchRegion(id+"F10",true);
            var Q1;
            Q1=sQuery(id+"F10.wireOp",EDGE,"E81");
            revolve(context, id + "F11", {"entities" : qUnion([Q0]), "axis" : qUnion([Q1]), "revolveType" : RevolveType.FULL});
        }
        {
            var Q0;
            Q0=makeQuery(id+"F1.opRevolve","SWEPT_FACE",FACE,{"disambiguationData":[OSD([sQuery(id+"F0.wireOp",EDGE,"E2")])]});
            var sketch = newSketch(context, id + "F12", { "sketchPlane" : qUnion([Q0])});
            skArc(sketch, "E82.0", {"start": v(-18.06, 29.98) * mm, "mid": v(-24.75, 24.75) * mm, "end": v(-29.98, 18.06) * mm});
            skLineSegment(sketch, "E83.0", {"start": v(-34.35, 47.08) * mm, "end": v(-18.86, 31.59) * mm, "construction": true});
            skArc(sketch, "E84.0", {"start": v(-18.86, 31.59) * mm, "mid": v(-14.67, 25.45) * mm, "end": v(-13.01, 18.2) * mm, "construction": true});
            skLineSegment(sketch, "E85.0", {"start": v(-30.42, 48.8) * mm, "end": v(-16.41, 34.8) * mm, "construction": true});
            skLineSegment(sketch, "E86.0", {"start": v(-13, 56.03) * mm, "end": v(-13, 36.21) * mm, "construction": true});
            skArc(sketch, "E87.0", {"start": v(-13, 36.21) * mm, "mid": v(-14.23, 34.37) * mm, "end": v(-16.41, 34.8) * mm, "construction": true});
            skArc(sketch, "E88.0", {"start": v(-18.2, 13.01) * mm, "mid": v(-25.45, 14.67) * mm, "end": v(-31.59, 18.86) * mm, "construction": true});
            skLineSegment(sketch, "E89.0", {"start": v(-47.08, 34.35) * mm, "end": v(-31.59, 18.86) * mm, "construction": true});
            skArc(sketch, "E90.0", {"start": v(-19.21, 31.23) * mm, "mid": v(-18.62, 30.62) * mm, "end": v(-18.06, 29.98) * mm});
            skLineSegment(sketch, "E90.1", {"start": v(-28.83, 40.85) * mm, "end": v(-19.21, 31.23) * mm});
            skLineSegment(sketch, "E91.0", {"start": v(-40.85, 28.83) * mm, "end": v(-31.23, 19.21) * mm});
            skArc(sketch, "E91.1", {"start": v(-29.98, 18.06) * mm, "mid": v(-30.62, 18.62) * mm, "end": v(-31.23, 19.21) * mm});
            skLineSegment(sketch, "E92.0", {"start": v(-13.5, 48.14) * mm, "end": v(-13.5, 36.21) * mm});
            skArc(sketch, "E92.1", {"start": v(-13.5, 36.21) * mm, "mid": v(-14.43, 34.83) * mm, "end": v(-16.06, 35.15) * mm});
            skLineSegment(sketch, "E92.2", {"start": v(-24.5, 43.59) * mm, "end": v(-16.06, 35.15) * mm});
            skArc(sketch, "E93.trimOffspring", {"start": v(-28.83, 40.85) * mm, "mid": v(-35.36, 35.36) * mm, "end": v(-40.85, 28.83) * mm});
            skArc(sketch, "E94", {"start": v(-13.5, 48.14) * mm, "mid": v(-19.13, 46.2) * mm, "end": v(-24.5, 43.59) * mm});
            skArc(sketch, "E95.1.0", {"start": v(-49.27, 8.5) * mm, "mid": v(-50, 0) * mm, "end": v(-49.27, -8.5) * mm});
            skArc(sketch, "E95.1.1", {"start": v(-33.97, 8.43) * mm, "mid": v(-35, 0) * mm, "end": v(-33.97, -8.43) * mm});
            skLineSegment(sketch, "E95.1.2", {"start": v(-49.27, -8.5) * mm, "end": v(-35.67, -8.5) * mm});
            skLineSegment(sketch, "E95.1.3", {"start": v(-49.27, 8.5) * mm, "end": v(-35.67, 8.5) * mm});
            skArc(sketch, "E95.1.4", {"start": v(-35.67, 8.5) * mm, "mid": v(-34.82, 8.48) * mm, "end": v(-33.97, 8.43) * mm});
            skArc(sketch, "E95.1.5", {"start": v(-33.97, -8.43) * mm, "mid": v(-34.82, -8.48) * mm, "end": v(-35.67, -8.5) * mm});
            skLineSegment(sketch, "E95.1.6", {"start": v(-48.14, 13.5) * mm, "end": v(-36.21, 13.5) * mm});
            skArc(sketch, "E95.1.7", {"start": v(-35.15, 16.06) * mm, "mid": v(-34.83, 14.43) * mm, "end": v(-36.21, 13.5) * mm});
            skLineSegment(sketch, "E95.1.8", {"start": v(-43.59, 24.5) * mm, "end": v(-35.15, 16.06) * mm});
            skArc(sketch, "E95.1.9", {"start": v(-43.59, 24.5) * mm, "mid": v(-46.2, 19.13) * mm, "end": v(-48.14, 13.5) * mm});
            skArc(sketch, "E95.2.0", {"start": v(-40.85, -28.83) * mm, "mid": v(-35.36, -35.36) * mm, "end": v(-28.83, -40.85) * mm});
            skArc(sketch, "E95.2.1", {"start": v(-29.98, -18.06) * mm, "mid": v(-24.75, -24.75) * mm, "end": v(-18.06, -29.98) * mm});
            skLineSegment(sketch, "E95.2.2", {"start": v(-28.83, -40.85) * mm, "end": v(-19.21, -31.23) * mm});
            skLineSegment(sketch, "E95.2.3", {"start": v(-40.85, -28.83) * mm, "end": v(-31.23, -19.21) * mm});
            skArc(sketch, "E95.2.4", {"start": v(-31.23, -19.21) * mm, "mid": v(-30.62, -18.62) * mm, "end": v(-29.98, -18.06) * mm});
            skArc(sketch, "E95.2.5", {"start": v(-18.06, -29.98) * mm, "mid": v(-18.62, -30.62) * mm, "end": v(-19.21, -31.23) * mm});
            skLineSegment(sketch, "E95.2.6", {"start": v(-43.59, -24.5) * mm, "end": v(-35.15, -16.06) * mm});
            skArc(sketch, "E95.2.7", {"start": v(-36.21, -13.5) * mm, "mid": v(-34.83, -14.43) * mm, "end": v(-35.15, -16.06) * mm});
            skLineSegment(sketch, "E95.2.8", {"start": v(-48.14, -13.5) * mm, "end": v(-36.21, -13.5) * mm});
            skArc(sketch, "E95.2.9", {"start": v(-48.14, -13.5) * mm, "mid": v(-46.2, -19.13) * mm, "end": v(-43.59, -24.5) * mm});
            skArc(sketch, "E95.3.0", {"start": v(-8.5, -49.27) * mm, "mid": v(0, -50) * mm, "end": v(8.5, -49.27) * mm});
            skArc(sketch, "E95.3.1", {"start": v(-8.43, -33.97) * mm, "mid": v(0, -35) * mm, "end": v(8.43, -33.97) * mm});
            skLineSegment(sketch, "E95.3.2", {"start": v(8.5, -49.27) * mm, "end": v(8.5, -35.67) * mm});
            skLineSegment(sketch, "E95.3.3", {"start": v(-8.5, -49.27) * mm, "end": v(-8.5, -35.67) * mm});
            skArc(sketch, "E95.3.4", {"start": v(-8.5, -35.67) * mm, "mid": v(-8.48, -34.82) * mm, "end": v(-8.43, -33.97) * mm});
            skArc(sketch, "E95.3.5", {"start": v(8.43, -33.97) * mm, "mid": v(8.48, -34.82) * mm, "end": v(8.5, -35.67) * mm});
            skLineSegment(sketch, "E95.3.6", {"start": v(-13.5, -48.14) * mm, "end": v(-13.5, -36.21) * mm});
            skArc(sketch, "E95.3.7", {"start": v(-16.06, -35.15) * mm, "mid": v(-14.43, -34.83) * mm, "end": v(-13.5, -36.21) * mm});
            skLineSegment(sketch, "E95.3.8", {"start": v(-24.5, -43.59) * mm, "end": v(-16.06, -35.15) * mm});
            skArc(sketch, "E95.3.9", {"start": v(-24.5, -43.59) * mm, "mid": v(-19.13, -46.2) * mm, "end": v(-13.5, -48.14) * mm});
            skArc(sketch, "E95.4.0", {"start": v(28.83, -40.85) * mm, "mid": v(35.36, -35.36) * mm, "end": v(40.85, -28.83) * mm});
            skArc(sketch, "E95.4.1", {"start": v(18.06, -29.98) * mm, "mid": v(24.75, -24.75) * mm, "end": v(29.98, -18.06) * mm});
            skLineSegment(sketch, "E95.4.2", {"start": v(40.85, -28.83) * mm, "end": v(31.23, -19.21) * mm});
            skLineSegment(sketch, "E95.4.3", {"start": v(28.83, -40.85) * mm, "end": v(19.21, -31.23) * mm});
            skArc(sketch, "E95.4.4", {"start": v(19.21, -31.23) * mm, "mid": v(18.62, -30.62) * mm, "end": v(18.06, -29.98) * mm});
            skArc(sketch, "E95.4.5", {"start": v(29.98, -18.06) * mm, "mid": v(30.62, -18.62) * mm, "end": v(31.23, -19.21) * mm});
            skLineSegment(sketch, "E95.4.6", {"start": v(24.5, -43.59) * mm, "end": v(16.06, -35.15) * mm});
            skArc(sketch, "E95.4.7", {"start": v(13.5, -36.21) * mm, "mid": v(14.43, -34.83) * mm, "end": v(16.06, -35.15) * mm});
            skLineSegment(sketch, "E95.4.8", {"start": v(13.5, -48.14) * mm, "end": v(13.5, -36.21) * mm});
            skArc(sketch, "E95.4.9", {"start": v(13.5, -48.14) * mm, "mid": v(19.13, -46.2) * mm, "end": v(24.5, -43.59) * mm});
            skArc(sketch, "E95.5.0", {"start": v(49.27, -8.5) * mm, "mid": v(50, 0) * mm, "end": v(49.27, 8.5) * mm});
            skArc(sketch, "E95.5.1", {"start": v(33.97, -8.43) * mm, "mid": v(35, 0) * mm, "end": v(33.97, 8.43) * mm});
            skLineSegment(sketch, "E95.5.2", {"start": v(49.27, 8.5) * mm, "end": v(35.67, 8.5) * mm});
            skLineSegment(sketch, "E95.5.3", {"start": v(49.27, -8.5) * mm, "end": v(35.67, -8.5) * mm});
            skArc(sketch, "E95.5.4", {"start": v(35.67, -8.5) * mm, "mid": v(34.82, -8.48) * mm, "end": v(33.97, -8.43) * mm});
            skArc(sketch, "E95.5.5", {"start": v(33.97, 8.43) * mm, "mid": v(34.82, 8.48) * mm, "end": v(35.67, 8.5) * mm});
            skLineSegment(sketch, "E95.5.6", {"start": v(48.14, -13.5) * mm, "end": v(36.21, -13.5) * mm});
            skArc(sketch, "E95.5.7", {"start": v(35.15, -16.06) * mm, "mid": v(34.83, -14.43) * mm, "end": v(36.21, -13.5) * mm});
            skLineSegment(sketch, "E95.5.8", {"start": v(43.59, -24.5) * mm, "end": v(35.15, -16.06) * mm});
            skArc(sketch, "E95.5.9", {"start": v(43.59, -24.5) * mm, "mid": v(46.2, -19.13) * mm, "end": v(48.14, -13.5) * mm});
            skArc(sketch, "E95.6.0", {"start": v(40.85, 28.83) * mm, "mid": v(35.36, 35.36) * mm, "end": v(28.83, 40.85) * mm});
            skArc(sketch, "E95.6.1", {"start": v(29.98, 18.06) * mm, "mid": v(24.75, 24.75) * mm, "end": v(18.06, 29.98) * mm});
            skLineSegment(sketch, "E95.6.2", {"start": v(28.83, 40.85) * mm, "end": v(19.21, 31.23) * mm});
            skLineSegment(sketch, "E95.6.3", {"start": v(40.85, 28.83) * mm, "end": v(31.23, 19.21) * mm});
            skArc(sketch, "E95.6.4", {"start": v(31.23, 19.21) * mm, "mid": v(30.62, 18.62) * mm, "end": v(29.98, 18.06) * mm});
            skArc(sketch, "E95.6.5", {"start": v(18.06, 29.98) * mm, "mid": v(18.62, 30.62) * mm, "end": v(19.21, 31.23) * mm});
            skLineSegment(sketch, "E95.6.6", {"start": v(43.59, 24.5) * mm, "end": v(35.15, 16.06) * mm});
            skArc(sketch, "E95.6.7", {"start": v(36.21, 13.5) * mm, "mid": v(34.83, 14.43) * mm, "end": v(35.15, 16.06) * mm});
            skLineSegment(sketch, "E95.6.8", {"start": v(48.14, 13.5) * mm, "end": v(36.21, 13.5) * mm});
            skArc(sketch, "E95.6.9", {"start": v(48.14, 13.5) * mm, "mid": v(46.2, 19.13) * mm, "end": v(43.59, 24.5) * mm});
            skArc(sketch, "E95.7.0", {"start": v(8.5, 49.27) * mm, "mid": v(0, 50) * mm, "end": v(-8.5, 49.27) * mm});
            skArc(sketch, "E95.7.1", {"start": v(8.43, 33.97) * mm, "mid": v(0, 35) * mm, "end": v(-8.43, 33.97) * mm});
            skLineSegment(sketch, "E95.7.2", {"start": v(-8.5, 49.27) * mm, "end": v(-8.5, 35.67) * mm});
            skLineSegment(sketch, "E95.7.3", {"start": v(8.5, 49.27) * mm, "end": v(8.5, 35.67) * mm});
            skArc(sketch, "E95.7.4", {"start": v(8.5, 35.67) * mm, "mid": v(8.48, 34.82) * mm, "end": v(8.43, 33.97) * mm});
            skArc(sketch, "E95.7.5", {"start": v(-8.43, 33.97) * mm, "mid": v(-8.48, 34.82) * mm, "end": v(-8.5, 35.67) * mm});
            skLineSegment(sketch, "E95.7.6", {"start": v(13.5, 48.14) * mm, "end": v(13.5, 36.21) * mm});
            skArc(sketch, "E95.7.7", {"start": v(16.06, 35.15) * mm, "mid": v(14.43, 34.83) * mm, "end": v(13.5, 36.21) * mm});
            skLineSegment(sketch, "E95.7.8", {"start": v(24.5, 43.59) * mm, "end": v(16.06, 35.15) * mm});
            skArc(sketch, "E95.7.9", {"start": v(24.5, 43.59) * mm, "mid": v(19.13, 46.2) * mm, "end": v(13.5, 48.14) * mm});
            skSolve(sketch);
        }
        {
            var Q0;
            Q0=qSketchRegion(id+"F12",true);
            extrude(context, id + "F13", {"entities" : qUnion([Q0]), "operationType" : NewBodyOperationType.ADD, "oppositeDirection" : true, "depth" : 4 * mm});
        }
        {
            var Q0;
            Q0=makeQuery(id+"F1.opRevolve","SWEPT_FACE",FACE,{"disambiguationData":[OSD([sQuery(id+"F0.wireOp",EDGE,"E2")])]});
            var sketch = newSketch(context, id + "F14", { "sketchPlane" : qUnion([Q0])});
            skCircle(sketch, "E96", {"center": v(0, 0) * mm, "radius": 72.4 * mm});
            skCircle(sketch, "E97.0", {"center": v(0, 0) * mm, "radius": 66 * mm});
            skSolve(sketch);
        }
        {
            var Q0;
            Q0=qSketchRegion(id+"F14",true);
            extrude(context, id + "F15", {"entities" : qUnion([Q0]), "operationType" : NewBodyOperationType.ADD, "oppositeDirection" : true, "depth" : 5.84 * mm});
        }
        {
            var Q0;
            Q0=makeQuery(id+"F15.opExtrude","CAP_EDGE",EDGE,{"disambiguationData":[OSD([sQuery(id+"F14.wireOp",EDGE,"E97.0")])],"isStart":false});
            var Q1;
            Q1=makeQuery(id+"F15.opExtrude","CAP_EDGE",EDGE,{"disambiguationData":[OSD([sQuery(id+"F14.wireOp",EDGE,"E96")])],"isStart":true});
            var Q2;
            Q2=makeQuery(id+"F15.opExtrude","CAP_EDGE",EDGE,{"disambiguationData":[OSD([sQuery(id+"F14.wireOp",EDGE,"E96")])],"isStart":false});
            fillet(context, id + "F16", {"entities" : qUnion([Q0, Q1, Q2]), "radius" : 1 * mm, "tangentPropagation" : true, "allowEdgeOverflow" : false});
        }
    });
